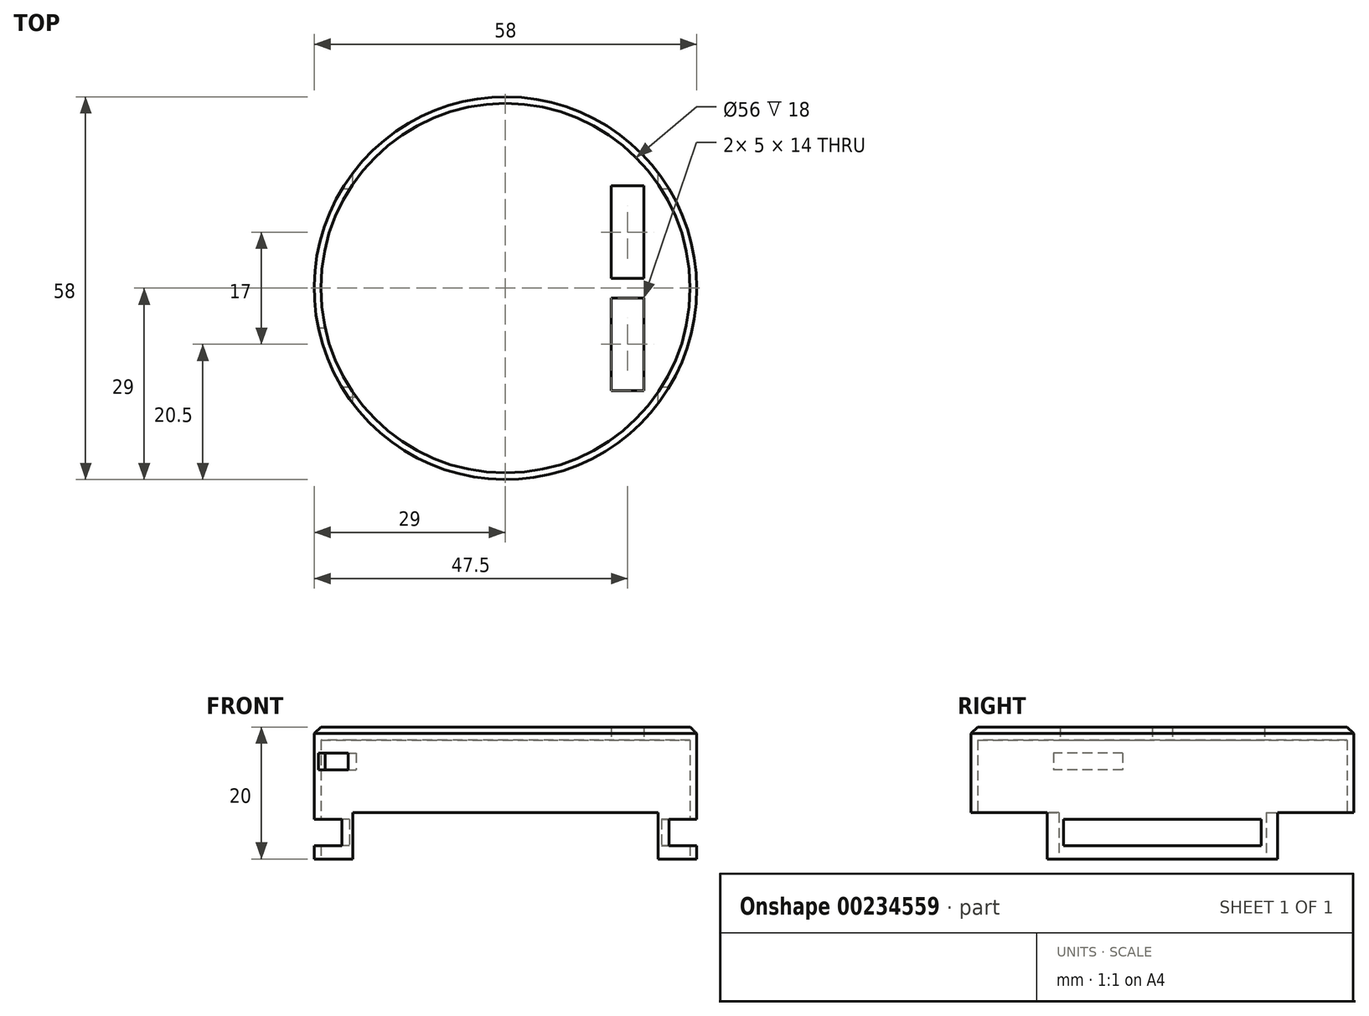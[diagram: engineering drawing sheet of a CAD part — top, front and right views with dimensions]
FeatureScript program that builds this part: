
annotation { "Feature Type Name" : "Feature", "Feature Type Description" : "" }
export const myFeature = defineFeature(function(context is Context, id is Id, definition is map)
    precondition{}
    {
        {
            var Q0;
            Q0=qCreatedBy(makeId("Top.planeOp"),FACE);
            var sketch = newSketch(context, id + "F0", { "sketchPlane" : qUnion([Q0])});
            skCircle(sketch, "E0", {"center": v(0, 0) * mm, "radius": 29 * mm});
            skSolve(sketch);
        }
        {
            var Q0;
            Q0=qCreatedBy(makeId("Top.planeOp"),FACE);
            var sketch = newSketch(context, id + "F1", { "sketchPlane" : qUnion([Q0])});
            skCircle(sketch, "E1", {"center": v(0, 0) * mm, "radius": 28 * mm});
            skSolve(sketch);
        }
        {
            var Q0;
            Q0=makeQuery(id+"F0.imprint","IMPRINT",FACE,{"disambiguationData":[TD([[makeQuery(id+"F0.imprint","IMPRINT",EDGE,{"derivedFrom":sQuery(id+"F0.wireOp",EDGE,"E0")}),1.0]])]});
            var sketch = newSketch(context, id + "F2", { "sketchPlane" : qUnion([Q0])});
            skLineSegment(sketch, "E2.bottom", {"start": v(16, 15.5) * mm, "end": v(21, 15.5) * mm});
            skLineSegment(sketch, "E2.top", {"start": v(16, 1.5) * mm, "end": v(21, 1.5) * mm});
            skLineSegment(sketch, "E2.left", {"start": v(16, 15.5) * mm, "end": v(16, 1.5) * mm});
            skLineSegment(sketch, "E2.right", {"start": v(21, 15.5) * mm, "end": v(21, 1.5) * mm});
            skLineSegment(sketch, "E3.bottom", {"start": v(16, -1.5) * mm, "end": v(21, -1.5) * mm});
            skLineSegment(sketch, "E3.top", {"start": v(16, -15.5) * mm, "end": v(21, -15.5) * mm});
            skLineSegment(sketch, "E3.left", {"start": v(16, -1.5) * mm, "end": v(16, -15.5) * mm});
            skLineSegment(sketch, "E3.right", {"start": v(21, -1.5) * mm, "end": v(21, -15.5) * mm});
            skPoint(sketch, "E4", {"position": v(-29, 10.54) * mm});
            skSolve(sketch);
        }
        {
            var Q0;
            Q0=qCreatedBy(makeId("Right.planeOp"),FACE);
            var sketch = newSketch(context, id + "F3", { "sketchPlane" : qUnion([Q0])});
            skLineSegment(sketch, "E5.bottom", {"start": v(-6, 16.05) * mm, "end": v(-16.5, 16.05) * mm});
            skLineSegment(sketch, "E5.top", {"start": v(-6, 13.5) * mm, "end": v(-16.5, 13.5) * mm});
            skLineSegment(sketch, "E5.left", {"start": v(-6, 16.05) * mm, "end": v(-6, 13.5) * mm});
            skLineSegment(sketch, "E5.right", {"start": v(-16.5, 16.05) * mm, "end": v(-16.5, 13.5) * mm});
            skLineSegment(sketch, "E6.bottom", {"start": v(29, 20) * mm, "end": v(-29, 20) * mm});
            skLineSegment(sketch, "E6.top", {"start": v(29, 0) * mm, "end": v(-29, 0) * mm});
            skLineSegment(sketch, "E6.left", {"start": v(29, 20) * mm, "end": v(29, 0) * mm});
            skLineSegment(sketch, "E6.right", {"start": v(-29, 20) * mm, "end": v(-29, 0) * mm});
            skSolve(sketch);
        }
        {
            var Q0;
            Q0 = qSketchRegion(id + "F0", true);
            extrude(context, id + "F4", {"entities" : qUnion([Q0]), "depth" : 20 * mm});
        }
        {
            var Q0;
            Q0=makeQuery(id+"F4.opExtrude","CAP_EDGE",EDGE,{"disambiguationData":[OSD([sQuery(id+"F0.wireOp",EDGE,"E0")])],"isStart":false});
            chamfer(context, id + "F5", {"entities" : qUnion([Q0]), "width" : 1 * mm, "tangentPropagation" : true});
        }
        {
            var Q0;
            Q0 = qSketchRegion(id + "F1", true);
            extrude(context, id + "F6", {"entities" : qUnion([Q0]), "operationType" : NewBodyOperationType.REMOVE, "depth" : 18 * mm});
        }
        {
            var Q0;
            Q0 = qSketchRegion(id + "F2", true);
            extrude(context, id + "F7", {"entities" : qUnion([Q0]), "operationType" : NewBodyOperationType.REMOVE, "depth" : 20.1 * mm});
        }
        {
            var Q0;
            Q0=makeQuery(id+"F3.imprint","IMPRINT",FACE,{"disambiguationData":[TD([[makeQuery(id+"F3.imprint","IMPRINT",EDGE,{"derivedFrom":sQuery(id+"F3.wireOp",EDGE,"E5.bottom")}),1.0]])]});
            extrude(context, id + "F8", {"entities" : qUnion([Q0]), "operationType" : NewBodyOperationType.REMOVE, "oppositeDirection" : true, "depth" : 42.4 * mm});
        }
        {
            var Q0;
            Q0=qCreatedBy(makeId("Top.planeOp"),FACE);
            var sketch = newSketch(context, id + "F9", { "sketchPlane" : qUnion([Q0])});
            skLineSegment(sketch, "E7.bottom", {"start": v(23.17, -32.6) * mm, "end": v(-23.17, -32.6) * mm});
            skLineSegment(sketch, "E7.top", {"start": v(23.17, 32.6) * mm, "end": v(-23.17, 32.6) * mm});
            skLineSegment(sketch, "E7.left", {"start": v(23.17, -32.6) * mm, "end": v(23.17, 32.6) * mm});
            skLineSegment(sketch, "E7.right", {"start": v(-23.17, -32.6) * mm, "end": v(-23.17, 32.6) * mm});
            skPoint(sketch, "E7.middle", {"position": v(0, 0) * mm});
            skSolve(sketch);
        }
        {
            var Q0;
            Q0 = qSketchRegion(id + "F9", true);
            extrude(context, id + "F10", {"entities" : qUnion([Q0]), "operationType" : NewBodyOperationType.REMOVE, "depth" : 7 * mm});
        }
        {
            var Q0;
            Q0=qCreatedBy(makeId("Right.planeOp"),FACE);
            var sketch = newSketch(context, id + "F11", { "sketchPlane" : qUnion([Q0])});
            skLineSegment(sketch, "E8.bottom", {"start": v(-15, 6) * mm, "end": v(15, 6) * mm});
            skLineSegment(sketch, "E8.top", {"start": v(-15, 2) * mm, "end": v(15, 2) * mm});
            skLineSegment(sketch, "E8.left", {"start": v(-15, 6) * mm, "end": v(-15, 2) * mm});
            skLineSegment(sketch, "E8.right", {"start": v(15, 6) * mm, "end": v(15, 2) * mm});
            skPoint(sketch, "E8.middle", {"position": v(0, 4) * mm});
            skSolve(sketch);
        }
        {
            var Q0;
            Q0 = qSketchRegion(id + "F11", true);
            extrude(context, id + "F12", {"entities" : qUnion([Q0]), "operationType" : NewBodyOperationType.REMOVE, "endBound" : BoundingType.SYMMETRIC, "depth" : 90 * mm});
        }
    });
